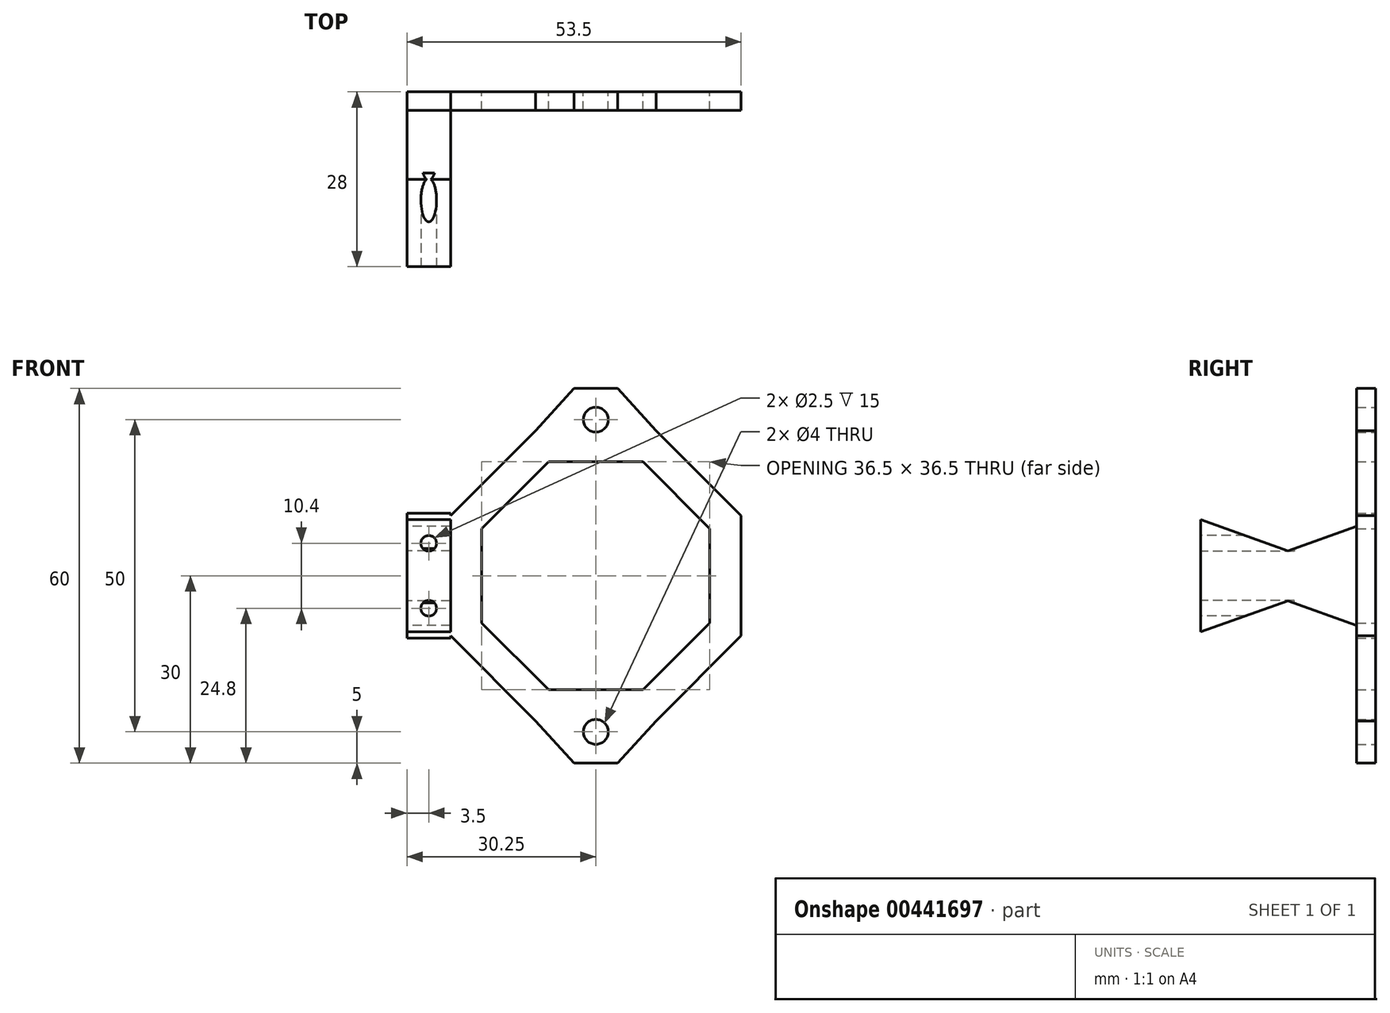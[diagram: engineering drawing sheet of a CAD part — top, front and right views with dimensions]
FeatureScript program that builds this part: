
annotation { "Feature Type Name" : "Feature", "Feature Type Description" : "" }
export const myFeature = defineFeature(function(context is Context, id is Id, definition is map)
    precondition{}
    {
        {
            var Q0;
            Q0=qCreatedBy(makeId("Front.planeOp"),FACE);
            var sketch = newSketch(context, id + "F0", { "sketchPlane" : qUnion([Q0])});
            skLineSegment(sketch, "E0", {"start": v(0, 39.11) * mm, "end": v(0, -38.7) * mm, "construction": true});
            skLineSegment(sketch, "E1", {"start": v(-45.07, 0) * mm, "end": v(60.02, 0) * mm, "construction": true});
            skCircle(sketch, "E2", {"center": v(0, 25) * mm, "radius": 2 * mm});
            skLineSegment(sketch, "E3", {"start": v(-16.72, 25) * mm, "end": v(14.78, 25) * mm, "construction": true});
            skLineSegment(sketch, "E4.MirrorCS", {"start": v(-16.72, -25) * mm, "end": v(14.78, -25) * mm, "construction": true});
            skCircle(sketch, "E5.MirrorC", {"center": v(0, -25) * mm, "radius": 2 * mm});
            skLineSegment(sketch, "E6", {"start": v(-3.5, 30) * mm, "end": v(3.5, 30) * mm});
            skLineSegment(sketch, "E7.MirrorCS", {"start": v(-3.5, -30) * mm, "end": v(3.5, -30) * mm});
            skCircle(sketch, "E8", {"center": v(0, 0) * mm, "radius": 18.25 * mm, "construction": true});
            skPoint(sketch, "E9.cCircle.perimeterSnap0", {"position": v(0, 19.5) * mm});
            skLineSegment(sketch, "E9.0", {"start": v(-7.56, 18.25) * mm, "end": v(7.56, 18.25) * mm});
            skLineSegment(sketch, "E9.1", {"start": v(7.56, 18.25) * mm, "end": v(18.25, 7.56) * mm});
            skLineSegment(sketch, "E9.2", {"start": v(18.25, 7.56) * mm, "end": v(18.25, -7.56) * mm});
            skLineSegment(sketch, "E9.3", {"start": v(18.25, -7.56) * mm, "end": v(7.56, -18.25) * mm});
            skLineSegment(sketch, "E9.4", {"start": v(7.56, -18.25) * mm, "end": v(-7.56, -18.25) * mm});
            skLineSegment(sketch, "E9.5", {"start": v(-7.56, -18.25) * mm, "end": v(-18.25, -7.56) * mm});
            skLineSegment(sketch, "E9.6", {"start": v(-18.25, -7.56) * mm, "end": v(-18.25, 7.56) * mm});
            skLineSegment(sketch, "E9.7", {"start": v(-18.25, 7.56) * mm, "end": v(-7.56, 18.25) * mm});
            skPoint(sketch, "E9.0.midPoint", {"position": v(0, 18.25) * mm});
            skPoint(sketch, "E9.0.midPoint.positionSnap0", {"position": v(0, 19.75) * mm});
            skCircle(sketch, "E10.cCircle", {"center": v(0, 0) * mm, "radius": 23.25 * mm, "construction": true});
            skLineSegment(sketch, "E10.0", {"start": v(-9.63, 23.25) * mm, "end": v(9.63, 23.25) * mm});
            skLineSegment(sketch, "E10.1", {"start": v(9.63, 23.25) * mm, "end": v(23.25, 9.63) * mm});
            skLineSegment(sketch, "E10.2", {"start": v(23.25, 9.63) * mm, "end": v(23.25, -9.63) * mm});
            skLineSegment(sketch, "E10.3", {"start": v(23.25, -9.63) * mm, "end": v(9.63, -23.25) * mm});
            skLineSegment(sketch, "E10.4", {"start": v(9.63, -23.25) * mm, "end": v(-9.63, -23.25) * mm});
            skLineSegment(sketch, "E10.5", {"start": v(-9.63, -23.25) * mm, "end": v(-23.25, -9.63) * mm});
            skLineSegment(sketch, "E10.6", {"start": v(-23.25, -9.63) * mm, "end": v(-23.25, 9.63) * mm});
            skLineSegment(sketch, "E10.7", {"start": v(-23.25, 9.63) * mm, "end": v(-9.63, 23.25) * mm});
            skPoint(sketch, "E10.0.midPoint", {"position": v(0, 23.25) * mm});
            skLineSegment(sketch, "E11", {"start": v(3.5, 30) * mm, "end": v(9.63, 23.25) * mm});
            skLineSegment(sketch, "E12", {"start": v(-3.5, 30) * mm, "end": v(-9.63, 23.25) * mm});
            skLineSegment(sketch, "E13.MirrorCS", {"start": v(-3.5, -30) * mm, "end": v(-9.63, -23.25) * mm});
            skLineSegment(sketch, "E14.MirrorCS", {"start": v(3.5, -30) * mm, "end": v(9.63, -23.25) * mm});
            skSolve(sketch);
        }
        {
            var Q0;
            Q0=qSketchRegion(id+"F0",true);
            extrude(context, id + "F1", {"entities" : qUnion([Q0]), "endBound" : BoundingType.SYMMETRIC, "depth" : 3 * mm, "offsetDistance" : 25 * mm});
        }
        {
            var Q0;
            {var subQ0=sQuery(id+"F0.wireOp",EDGE,"9ce0b469-3e6d-4484-9b44-6347bf59e3190.MirrorCS");var subQ2=sQuery(id+"F0.wireOp",EDGE,"5970f104-e2bd-4247-84a5-b9d6516839af0.MirrorCS");var subQ4=sQuery(id+"F0.wireOp",EDGE,"904158f1-41e8-4349-8dac-cfb45db5622d0.MirrorCS");var subQ6=sQuery(id+"F0.wireOp",EDGE,"83K7zddE-VT2C-bhFO-M99s-P2ZDVPqol09J");var subQ8=sQuery(id+"F0.wireOp",EDGE,"8fa62911-e7d8-4df8-927e-ab7da559bd730.MirrorCS");var subQ10=sQuery(id+"F0.wireOp",EDGE,"3f95e314-f86e-4096-bca5-a87affd907cb0.MirrorCS");var subQ12=sQuery(id+"F0.wireOp",EDGE,"8bd424dc-a5d5-43a6-bfb8-db73a6b3af220.MirrorCS");var subQ14=sQuery(id+"F0.wireOp",EDGE,"665ac0ac-0af9-4c5b-90df-9ef42098dc210.MirrorCS");var subQ16=sQuery(id+"F0.wireOp",EDGE,"30e28cb9-c2be-4751-92ca-3f74ec1cadfd0.MirrorCS");var subQ18=sQuery(id+"F0.wireOp",EDGE,"WVCh4hOS-V3ar-SxM0-pMMq-p7c69A6RROSp");var subQ20=sQuery(id+"F0.wireOp",EDGE,"vbZjeP3O-W9Lq-FhQq-uazA-jM45rhWqh3rV");var subQ24=sQuery(id+"F0.wireOp",EDGE,"H0qez70T-8V3A-99WH-qXad-sgiO0mYvdILm");var subQ25=makeQuery(id+"F1.opExtrude","SWEPT_FACE",FACE,{"disambiguationData":[OSD([subQ24])]});var subQ26=sQuery(id+"F0.wireOp",EDGE,"E7.MirrorCS");var subQ27=sQuery(id+"F0.wireOp",EDGE,"c0dd41b9-1cc2-4414-b6c9-18af5a17e1af0.MirrorCS");var subQ28=sQuery(id+"F0.wireOp",EDGE,"2f12a7ed-1dd8-4c5d-8766-3f1364a963af0.MirrorCS");var subQ29=sQuery(id+"F0.wireOp",EDGE,"BqpGEcAr-iL5O-eIYc-LFqk-zhXzDYrk6e3o");var subQ30=sQuery(id+"F0.wireOp",EDGE,"qyGAIO29-i2jA-uRhJ-LdBd-cRcclpV66Y8K");var subQ31=sQuery(id+"F0.wireOp",EDGE,"qLRKDBQW-Isje-sjCA-rkLo-dmmEErss2v6p");var subQ32=sQuery(id+"F0.wireOp",EDGE,"aykP4BTx-FQj5-qn8E-jsu9-MW0GS4yRGmX5");var subQ33=sQuery(id+"F0.wireOp",EDGE,"E5.MirrorC");var subQ34=makeQuery(id+"F1.opExtrude","CAP_FACE",FACE,{"disambiguationData":[OSD([sQuery(id+"F0.wireOp",EDGE,"E2"),subQ33,subQ24,subQ20,subQ18,subQ32,subQ31,subQ30,subQ29,subQ28,subQ27,subQ16,subQ14,subQ12,subQ10,subQ8,subQ6,subQ4,sQuery(id+"F0.wireOp",EDGE,"E6"),subQ26,subQ2,subQ0])],"isStart":false});Q0=makeQuery(id+"FprA0KHaE6P31Dc_1.1.F4oyRz6wdiwPSX1_1.boolean.opBoolean","SPLIT",FACE,{"disambiguationData":[TD([subQ25])],"derivedFrom":makeQuery(id+"F4oyRz6wdiwPSX1_1.boolean.opBoolean","SPLIT",FACE,{"disambiguationData":[TD([makeQuery(id+"F1.opExtrude","SWEPT_FACE",FACE,{"disambiguationData":[OSD([subQ33])]})])],"derivedFrom":subQ34})});}
            var sketch = newSketch(context, id + "F2", { "sketchPlane" : qUnion([Q0])});
            skLineSegment(sketch, "E15", {"start": v(0, -34.06) * mm, "end": v(0, -2.07) * mm, "construction": true});
            skSolve(sketch);
        }
        {
            var Q0;
            Q0=makeQuery(id+"F2.imprint","IMPRINT",FACE,{"disambiguationData":[TD([[makeQuery(id+"F2.imprint","IMPRINT",EDGE,{"derivedFrom":makeQuery(id+"F1.opExtrude","CAP_EDGE",EDGE,{"disambiguationData":[OSD([sQuery(id+"F0.wireOp",EDGE,"E2")])],"isStart":false})}),-1.0]])]});
            var sketch = newSketch(context, id + "F3", { "sketchPlane" : qUnion([Q0])});
            skLineSegment(sketch, "E16", {"start": v(-23.25, 10) * mm, "end": v(-30.25, 10) * mm});
            skLineSegment(sketch, "E17", {"start": v(-23.25, 10) * mm, "end": v(-23.25, -10) * mm});
            skLineSegment(sketch, "E18", {"start": v(-30.25, -10) * mm, "end": v(-23.25, -10) * mm});
            skLineSegment(sketch, "E19", {"start": v(-30.25, -10) * mm, "end": v(-30.25, 10) * mm});
            skLineSegment(sketch, "E20", {"start": v(-43.16, 0) * mm, "end": v(45.75, 0) * mm, "construction": true});
            skLineSegment(sketch, "E21", {"start": v(-26.75, 15.72) * mm, "end": v(-26.75, -15.73) * mm, "construction": true});
            skSolve(sketch);
        }
        {
            var Q0;
            Q0 = qSketchRegion(id + "F3", true);
            extrude(context, id + "F4", {"entities" : qUnion([Q0]), "operationType" : NewBodyOperationType.ADD, "depth" : 25 * mm, "offsetDistance" : 25 * mm});
        }
        {
            var Q0;
            Q0=makeQuery(id+"F4.opExtrude","CAP_FACE",FACE,{"disambiguationData":[OSD([sQuery(id+"F3.wireOp",EDGE,"E16"),sQuery(id+"F3.wireOp",EDGE,"E17"),sQuery(id+"F3.wireOp",EDGE,"E18"),sQuery(id+"F3.wireOp",EDGE,"E19")])],"isStart":false});
            var sketch = newSketch(context, id + "F5", { "sketchPlane" : qUnion([Q0])});
            skLineSegment(sketch, "E22", {"start": v(-40.17, 0) * mm, "end": v(-13.63, 0) * mm, "construction": true});
            skLineSegment(sketch, "E23", {"start": v(-26.75, 14.4) * mm, "end": v(-26.75, -13.9) * mm, "construction": true});
            skCircle(sketch, "E24", {"center": v(-26.75, 5.2) * mm, "radius": 1.25 * mm});
            skCircle(sketch, "E25.MirrorC", {"center": v(-26.75, -5.2) * mm, "radius": 1.25 * mm});
            skSolve(sketch);
        }
        {
            var Q0;
            Q0 = qSketchRegion(id + "F5", true);
            extrude(context, id + "F6", {"entities" : qUnion([Q0]), "operationType" : NewBodyOperationType.REMOVE, "oppositeDirection" : true, "depth" : 15 * mm, "offsetDistance" : 25 * mm});
        }
        {
            var Q0;
            {var subQ2=sQuery(id+"F0.wireOp",EDGE,"E10.5");var subQ3=sQuery(id+"F3.wireOp",EDGE,"E16");var subQ4=sQuery(id+"F3.wireOp",EDGE,"E18");var subQ5=sQuery(id+"F3.wireOp",EDGE,"E19");Q0=makeQuery(id+"F4.boolean.opBoolean","SPLIT",FACE,{"disambiguationData":[TD([makeQuery(id+"F1.opExtrude","SWEPT_FACE",FACE,{"disambiguationData":[OSD([subQ2])]})])],"derivedFrom":makeQuery(id+"F4.opExtrude","CAP_FACE",FACE,{"disambiguationData":[OSD([subQ3,sQuery(id+"F3.wireOp",EDGE,"E17"),subQ4,subQ5])],"isStart":true})});}
            var Q1;
            Q1=makeQuery(id+"F1.opExtrude","CAP_FACE",FACE,{"disambiguationData":[OSD([sQuery(id+"F0.wireOp",EDGE,"E2"),sQuery(id+"F0.wireOp",EDGE,"E5.MirrorC"),sQuery(id+"F0.wireOp",EDGE,"E6"),sQuery(id+"F0.wireOp",EDGE,"E7.MirrorCS"),sQuery(id+"F0.wireOp",EDGE,"E9.0"),sQuery(id+"F0.wireOp",EDGE,"E9.1"),sQuery(id+"F0.wireOp",EDGE,"E9.2"),sQuery(id+"F0.wireOp",EDGE,"E9.3"),sQuery(id+"F0.wireOp",EDGE,"E9.4"),sQuery(id+"F0.wireOp",EDGE,"E9.5"),sQuery(id+"F0.wireOp",EDGE,"E9.6"),sQuery(id+"F0.wireOp",EDGE,"E9.7"),sQuery(id+"F0.wireOp",EDGE,"E10.1"),sQuery(id+"F0.wireOp",EDGE,"E10.2"),sQuery(id+"F0.wireOp",EDGE,"E10.3"),sQuery(id+"F0.wireOp",EDGE,"E10.5"),sQuery(id+"F0.wireOp",EDGE,"E10.6"),sQuery(id+"F0.wireOp",EDGE,"E10.7"),sQuery(id+"F0.wireOp",EDGE,"E11"),sQuery(id+"F0.wireOp",EDGE,"E12"),sQuery(id+"F0.wireOp",EDGE,"E13.MirrorCS"),sQuery(id+"F0.wireOp",EDGE,"E14.MirrorCS")])],"isStart":true});
            extrude(context, id + "F7", {"entities" : qUnion([Q0]), "operationType" : NewBodyOperationType.ADD, "endBound" : BoundingType.UP_TO_SURFACE, "depth" : 25 * mm, "endBoundEntityFace" : qUnion([Q1]), "offsetDistance" : 25 * mm});
        }
        {
            var Q0;
            {var subQ0=sQuery(id+"F3.wireOp",EDGE,"E19");Q0=makeQuery(id+"F7.boolean.opBoolean","MERGE",FACE,{"derivedFrom":[makeQuery(id+"F4.opExtrude","SWEPT_FACE",FACE,{"disambiguationData":[OSD([subQ0])]}),makeQuery(id+"F7.opExtrude","SWEPT_FACE",FACE,{"disambiguationData":[OSD([subQ0])]})]});}
            var sketch = newSketch(context, id + "F8", { "sketchPlane" : qUnion([Q0])});
            skLineSegment(sketch, "E26", {"start": v(-5.86, 0) * mm, "end": v(35.59, 0) * mm, "construction": true});
            skLineSegment(sketch, "E27", {"start": v(-1.5, 9) * mm, "end": v(12.5, 4) * mm});
            skLineSegment(sketch, "E28", {"start": v(12.5, 4) * mm, "end": v(26.5, 9) * mm});
            skLineSegment(sketch, "E29", {"start": v(-1.5, -9) * mm, "end": v(12.5, -4) * mm});
            skLineSegment(sketch, "E30", {"start": v(12.5, -4) * mm, "end": v(26.5, -9) * mm});
            skLineSegment(sketch, "E31", {"start": v(12.5, 15.36) * mm, "end": v(12.5, -14.53) * mm, "construction": true});
            skLineSegment(sketch, "E32", {"start": v(1.5, 10) * mm, "end": v(1.5, -10) * mm});
            skSolve(sketch);
        }
        {
            var Q0;
            {var subQ5=sQuery(id+"F8.wireOp",EDGE,"E28");Q0=makeQuery(id+"F8.imprint","IMPRINT",FACE,{"disambiguationData":[TD([[makeQuery(id+"F8.imprint","IMPRINT",EDGE,{"derivedFrom":subQ5}),1.0]])]});}
            var Q1;
            {var subQ9=sQuery(id+"F8.wireOp",EDGE,"E30");Q1=makeQuery(id+"F8.imprint","IMPRINT",FACE,{"disambiguationData":[TD([[makeQuery(id+"F8.imprint","IMPRINT",EDGE,{"derivedFrom":subQ9}),-1.0]])]});}
            extrude(context, id + "F9", {"entities" : qUnion([Q0, Q1]), "operationType" : NewBodyOperationType.REMOVE, "endBound" : BoundingType.THROUGH_ALL, "oppositeDirection" : true, "depth" : 25 * mm, "offsetDistance" : 25 * mm});
        }
    });
